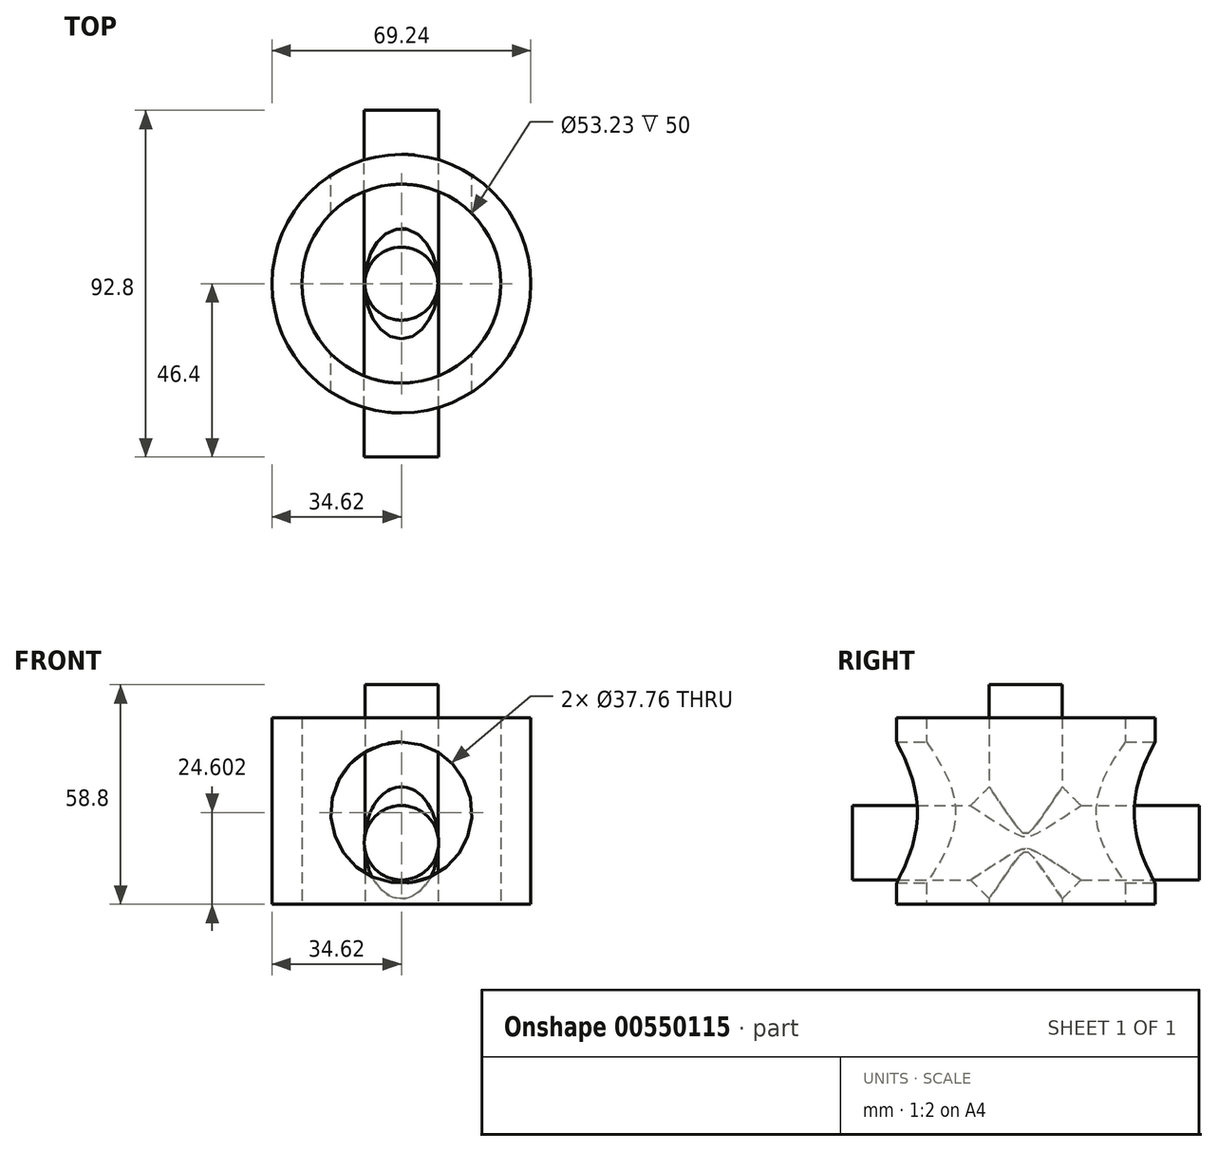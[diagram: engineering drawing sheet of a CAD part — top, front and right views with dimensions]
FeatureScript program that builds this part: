
annotation { "Feature Type Name" : "Feature", "Feature Type Description" : "" }
export const myFeature = defineFeature(function(context is Context, id is Id, definition is map)
    precondition{}
    {
        {
            var Q0;
            Q0=qCreatedBy(makeId("Top.planeOp"),FACE);
            var sketch = newSketch(context, id + "F0", { "sketchPlane" : qUnion([Q0])});
            skCircle(sketch, "E0", {"center": v(0, 0) * mm, "radius": 34.62 * mm});
            skCircle(sketch, "E1", {"center": v(0, 0) * mm, "radius": 26.62 * mm});
            skSolve(sketch);
        }
        {
            var Q0;
            Q0=makeQuery(id+"F0.imprint","IMPRINT",FACE,{"disambiguationData":[TD([[makeQuery(id+"F0.imprint","IMPRINT",EDGE,{"derivedFrom":sQuery(id+"F0.wireOp",EDGE,"E0")}),1.0]])]});
            extrude(context, id + "F1", {"entities" : qUnion([Q0]), "depth" : 50 * mm, "offsetDistance" : 25 * mm});
        }
        {
            var Q0;
            Q0=qCreatedBy(makeId("Front.planeOp"),FACE);
            var sketch = newSketch(context, id + "F2", { "sketchPlane" : qUnion([Q0])});
            skLineSegment(sketch, "E2", {"start": v(0, 0) * mm, "end": v(0, 24.6) * mm, "construction": true});
            skCircle(sketch, "E3", {"center": v(0, 24.6) * mm, "radius": 18.88 * mm});
            skSolve(sketch);
        }
        {
            var Q0;
            Q0=makeQuery(id+"F2.imprint","IMPRINT",FACE,{"disambiguationData":[TD([[makeQuery(id+"F2.imprint","IMPRINT",EDGE,{"derivedFrom":sQuery(id+"F2.wireOp",EDGE,"E3")}),1.0]])]});
            var Q1;
            Q1=sQuery(id+"F2.wireOp",EDGE,"E3");
            extrude(context, id + "F3", {"entities" : qUnion([Q0]), "operationType" : NewBodyOperationType.REMOVE, "surfaceEntities" : qUnion([Q1]), "endBound" : BoundingType.SYMMETRIC, "depth" : 100 * mm, "offsetDistance" : 25 * mm});
        }
        {
            var Q0;
            Q0=qCreatedBy(makeId("Front.planeOp"),FACE);
            var sketch = newSketch(context, id + "F4", { "sketchPlane" : qUnion([Q0])});
            skLineSegment(sketch, "E4", {"start": v(0, 0) * mm, "end": v(0, 16.5) * mm, "construction": true});
            skCircle(sketch, "E5", {"center": v(0, 16.5) * mm, "radius": 9.96 * mm});
            skSolve(sketch);
        }
        {
            var Q0;
            Q0=makeQuery(id+"F4.imprint","IMPRINT",FACE,{"disambiguationData":[TD([[makeQuery(id+"F4.imprint","IMPRINT",EDGE,{"derivedFrom":sQuery(id+"F4.wireOp",EDGE,"E5")}),1.0]])]});
            extrude(context, id + "F5", {"entities" : qUnion([Q0]), "endBound" : BoundingType.SYMMETRIC, "depth" : 92.8 * mm, "offsetDistance" : 25 * mm});
        }
        {
            var Q0;
            Q0=qCreatedBy(makeId("Top.planeOp"),FACE);
            var sketch = newSketch(context, id + "F6", { "sketchPlane" : qUnion([Q0])});
            skCircle(sketch, "E6", {"center": v(0, 0) * mm, "radius": 9.77 * mm});
            skSolve(sketch);
        }
        {
            var Q0;
            Q0=makeQuery(id+"F6.imprint","IMPRINT",FACE,{"disambiguationData":[TD([[makeQuery(id+"F6.imprint","IMPRINT",EDGE,{"derivedFrom":sQuery(id+"F6.wireOp",EDGE,"E6")}),1.0]])]});
            var Q1;
            Q1=sQuery(id+"F6.wireOp",EDGE,"E6");
            extrude(context, id + "F7", {"entities" : qUnion([Q0]), "operationType" : NewBodyOperationType.ADD, "surfaceEntities" : qUnion([Q1]), "depth" : 58.8 * mm, "offsetDistance" : 25 * mm});
        }
        {
            var Q0;
            Q0=makeQuery(id+"F7.boolean.opBoolean","INTERSECT",EDGE,{"disambiguationData":[OD(1.0)],"derivedFrom":[makeQuery(id+"F5.opExtrude","SWEPT_FACE",FACE,{"disambiguationData":[OSD([sQuery(id+"F4.wireOp",EDGE,"E5")])]}),makeQuery(id+"F7.opExtrude","SWEPT_FACE",FACE,{"disambiguationData":[OSD([sQuery(id+"F6.wireOp",EDGE,"E6")])]})]});
            var Q1;
            Q1=makeQuery(id+"F7.boolean.opBoolean","INTERSECT",EDGE,{"disambiguationData":[OD(0.0)],"derivedFrom":[makeQuery(id+"F5.opExtrude","SWEPT_FACE",FACE,{"disambiguationData":[OSD([sQuery(id+"F4.wireOp",EDGE,"E5")])]}),makeQuery(id+"F7.opExtrude","SWEPT_FACE",FACE,{"disambiguationData":[OSD([sQuery(id+"F6.wireOp",EDGE,"E6")])]})]});
            chamfer(context, id + "F8", {"entities" : qUnion([Q0, Q1]), "width" : 5 * mm, "tangentPropagation" : true});
        }
    });
